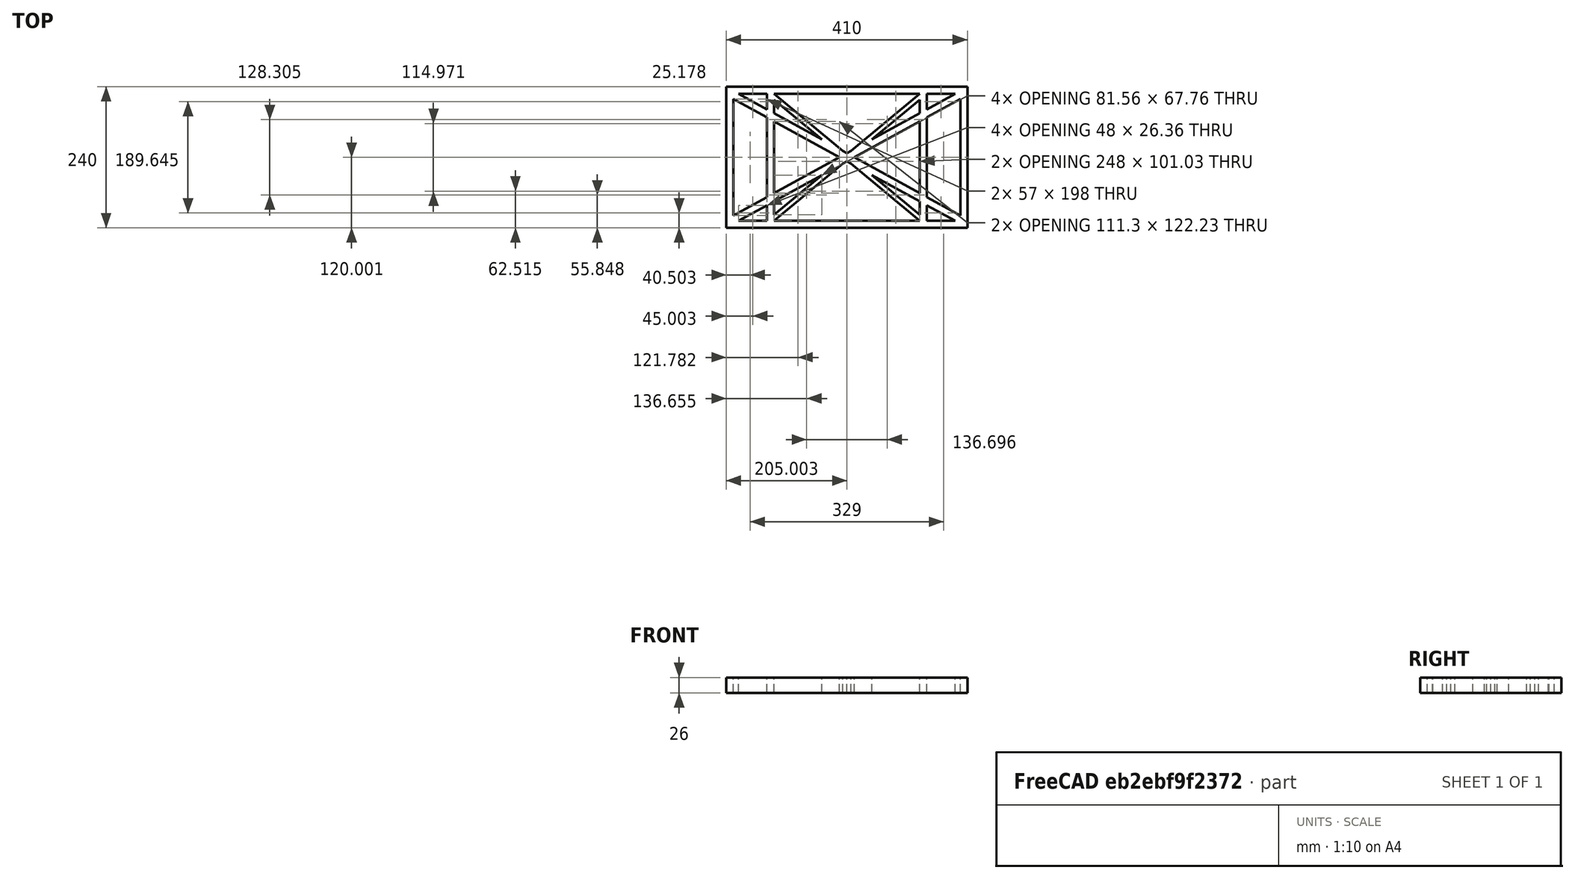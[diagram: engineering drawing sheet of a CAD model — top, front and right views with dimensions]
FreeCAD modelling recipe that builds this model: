
FCSTD DOCUMENT  (FreeCAD 0.19R0.19.2)
Label: laptopStand032
License: All rights reserved
LicenseURL: http://en.wikipedia.org/wiki/All_rights_reserved
objects: Sketcher::SketchObject×3, Part::Extrusion×1
note: 4 computed .brp shape members not serialized (recipe doc carries the construction recipe); baked Part::Feature solids carry a one-line shape summary decoded from their .brp

FEATURE [Sketcher::SketchObject] Sketch
  FullyConstrained = true
  sketch-geometry (52):
    g0: LineSegment StartX=-22.9272 StartY=136.221 StartZ=0 EndX=-22.9272 EndY=-103.779 EndZ=0
    g1: LineSegment StartX=-22.9272 StartY=136.221 StartZ=0 EndX=387.073 EndY=136.221 EndZ=0
    g2: LineSegment StartX=-22.9272 StartY=-103.779 StartZ=0 EndX=387.073 EndY=-103.779 EndZ=0
    g3: LineSegment StartX=387.073 StartY=136.221 StartZ=0 EndX=387.073 EndY=-103.779 EndZ=0
    g4: LineSegment StartX=375.073 StartY=115.221 StartZ=0 EndX=318.073 EndY=83.9235 EndZ=0
    g5: LineSegment StartX=-10.9272 StartY=-82.7794 StartZ=0 EndX=46.0728 EndY=-51.4823 EndZ=0
    g6: LineSegment StartX=-1.92719 StartY=124.221 StartZ=0 EndX=46.0728 EndY=97.8651 EndZ=0
    g7: LineSegment StartX=366.073 StartY=-91.7794 StartZ=0 EndX=318.073 EndY=-65.424 EndZ=0
    g8: LineSegment StartX=-10.9272 StartY=115.221 StartZ=0 EndX=-10.9272 EndY=-82.7794 EndZ=0
    g9: LineSegment StartX=375.073 StartY=-82.7794 StartZ=0 EndX=375.073 EndY=115.221 EndZ=0
    g10: LineSegment StartX=-1.92719 StartY=-91.7794 StartZ=0 EndX=46.0728 EndY=-91.7794 EndZ=0
    g11: LineSegment StartX=318.073 StartY=124.221 StartZ=0 EndX=366.073 EndY=124.221 EndZ=0
    g12: LineSegment StartX=306.073 StartY=-81.8102 StartZ=0 EndX=224.513 EndY=-14.0532 EndZ=0
    g13: LineSegment StartX=58.0728 StartY=114.251 StartZ=0 EndX=139.632 EndY=46.4944 EndZ=0
    g14: LineSegment StartX=306.073 StartY=124.221 StartZ=0 EndX=189.124 EndY=27.0628 EndZ=0
    g15: LineSegment StartX=58.0728 StartY=-91.7794 StartZ=0 EndX=175.022 EndY=5.37834 EndZ=0
    g16: LineSegment StartX=46.0728 StartY=124.221 StartZ=0 EndX=46.0728 EndY=97.8651 EndZ=0
    g17: LineSegment StartX=58.0728 StartY=-81.8102 StartZ=0 EndX=58.0728 EndY=-58.8351 EndZ=0
    g18: LineSegment StartX=318.073 StartY=124.221 StartZ=0 EndX=318.073 EndY=97.8651 EndZ=0
    g19: LineSegment StartX=306.073 StartY=114.251 StartZ=0 EndX=306.073 EndY=91.2763 EndZ=0
    g20: LineSegment StartX=182.073 StartY=23.1914 StartZ=0 EndX=189.124 EndY=27.0628 EndZ=0
    g21: LineSegment StartX=182.073 StartY=9.24976 StartZ=0 EndX=175.022 EndY=5.37834 EndZ=0
    g22: LineSegment StartX=224.513 StartY=46.4944 StartZ=0 EndX=306.073 EndY=114.251 EndZ=0
    g23: LineSegment StartX=175.022 StartY=27.0628 StartZ=0 EndX=58.0728 EndY=124.221 EndZ=0
    g24: LineSegment StartX=169.377 StartY=16.2206 StartZ=0 EndX=58.0728 EndY=77.3346 EndZ=0
    g25: LineSegment StartX=139.632 StartY=-14.0532 StartZ=0 EndX=58.0728 EndY=-81.8102 EndZ=0
    g26: LineSegment StartX=194.768 StartY=16.2206 StartZ=0 EndX=306.073 EndY=-44.8935 EndZ=0
    g27: LineSegment StartX=224.513 StartY=46.4944 StartZ=0 EndX=306.073 EndY=91.2763 EndZ=0
    g28: LineSegment StartX=175.022 StartY=27.0628 StartZ=0 EndX=182.073 EndY=23.1914 EndZ=0
    g29: LineSegment StartX=139.632 StartY=-14.0532 StartZ=0 EndX=58.0728 EndY=-58.8351 EndZ=0
    g30: LineSegment StartX=189.124 StartY=5.37834 StartZ=0 EndX=182.073 EndY=9.24976 EndZ=0
    g31: LineSegment StartX=189.124 StartY=5.37834 StartZ=0 EndX=306.073 EndY=-91.7794 EndZ=0
    g32: LineSegment StartX=306.073 StartY=77.3346 StartZ=0 EndX=306.073 EndY=-44.8935 EndZ=0
    g33: LineSegment StartX=318.073 StartY=83.9235 StartZ=0 EndX=318.073 EndY=-51.4823 EndZ=0
    g34: LineSegment StartX=318.073 StartY=97.8651 StartZ=0 EndX=366.073 EndY=124.221 EndZ=0
    g35: LineSegment StartX=306.073 StartY=77.3346 StartZ=0 EndX=194.768 EndY=16.2206 EndZ=0
    g36: LineSegment StartX=306.073 StartY=-58.8351 StartZ=0 EndX=224.513 EndY=-14.0532 EndZ=0
    g37: LineSegment StartX=306.073 StartY=-58.8351 StartZ=0 EndX=306.073 EndY=-81.8102 EndZ=0
    g38: LineSegment StartX=318.073 StartY=-51.4823 StartZ=0 EndX=375.073 EndY=-82.7794 EndZ=0
    g39: LineSegment StartX=318.073 StartY=-65.424 StartZ=0 EndX=318.073 EndY=-91.7794 EndZ=0
    g40: LineSegment StartX=306.073 StartY=124.221 StartZ=0 EndX=58.0728 EndY=124.221 EndZ=0
    g41: LineSegment StartX=318.073 StartY=-91.7794 StartZ=0 EndX=366.073 EndY=-91.7794 EndZ=0
    g42: LineSegment StartX=58.0728 StartY=-91.7794 StartZ=0 EndX=306.073 EndY=-91.7794 EndZ=0
    g43: LineSegment StartX=58.0728 StartY=-44.8935 StartZ=0 EndX=58.0728 EndY=77.3346 EndZ=0
    g44: LineSegment StartX=46.0728 StartY=-65.424 StartZ=0 EndX=-1.92719 EndY=-91.7794 EndZ=0
    g45: LineSegment StartX=46.0728 StartY=-65.424 StartZ=0 EndX=46.0728 EndY=-91.7794 EndZ=0
    g46: LineSegment StartX=58.0728 StartY=-44.8935 StartZ=0 EndX=169.377 EndY=16.2206 EndZ=0
    g47: LineSegment StartX=58.0728 StartY=91.2763 StartZ=0 EndX=58.0728 EndY=114.251 EndZ=0
    g48: LineSegment StartX=46.0728 StartY=83.9235 StartZ=0 EndX=46.0728 EndY=-51.4823 EndZ=0
    g49: LineSegment StartX=46.0728 StartY=124.221 StartZ=0 EndX=-1.92719 EndY=124.221 EndZ=0
    g50: LineSegment StartX=58.0728 StartY=91.2763 StartZ=0 EndX=139.632 EndY=46.4944 EndZ=0
    g51: LineSegment StartX=46.0728 StartY=83.9235 StartZ=0 EndX=-10.9272 EndY=115.221 EndZ=0
  constraints (102):
    c: Vertical(g0)
    c: Distance(g0) = 240
    c: Horizontal(g1)
    c: Distance(g1) = 410
    c: Coincident(g1,g0)
    c: Coincident(g2,g0)
    c: Horizontal(g2)
    c: Coincident(g3,g1)
    c: Vertical(g3)
    c: Coincident(g2,g3)
    c: Block(g1)
    c: Horizontal(g10)
    c: Horizontal(g11)
    c: PointOnObject(g35,g6)
    c: Coincident(g28,g20)
    c: Coincident(g30,g21)
    c: Tangent(g7,g24)
    c: PointOnObject(g24,g5)
    c: PointOnObject(g26,g4)
    c: Coincident(g20,g14)
    c: Tangent(g20,g27)
    c: Coincident(g50,g13)
    c: Coincident(g28,g23)
    c: Coincident(g22,g27)
    c: Coincident(g21,g15)
    c: Coincident(g29,g25)
    c: Tangent(g21,g29)
    c: Coincident(g36,g12)
    c: Coincident(g31,g30)
    c: Coincident(g22,g19)
    c: Tangent(g19,g32)
    c: Tangent(g18,g33)
    c: Coincident(g27,g19)
    c: Tangent(g27,g34)
    c: Coincident(g4,g33)
    c: Coincident(g35,g32)
    c: Tangent(g4,g35)
    c: Coincident(g37,g12)
    c: Tangent(g7,g36)
    c: Tangent(g32,g37)
    c: Coincident(g26,g32)
    c: Tangent(g26,g38)
    c: Coincident(g33,g38)
    c: Coincident(g39,g7)
    c: Tangent(g33,g39)
    c: Coincident(g25,g17)
    c: Tangent(g17,g43)
    c: Coincident(g29,g17)
    c: Tangent(g29,g44)
    c: Coincident(g45,g44)
    c: Tangent(g16,g45)
    c: Coincident(g5,g48)
    c: Coincident(g46,g43)
    c: Tangent(g5,g46)
    c: Tangent(g43,g47)
    c: Tangent(g16,g48)
    c: Coincident(g13,g47)
    c: PointOnObject(g40,g23)
    c: Tangent(g40,g49)
    c: Coincident(g6,g16)
    c: Coincident(g50,g47)
    c: Tangent(g6,g50)
    c: Coincident(g24,g43)
    c: Coincident(g51,g48)
    c: Tangent(g24,g51)
    c: Block(g23)
    c: Block(g14)
    c: Block(g20)
    c: Block(g40)
    c: Block(g18)
    c: Block(g34)
    c: Block(g4)
    c: Block(g38)
    c: Block(g9)
    c: Block(g36)
    c: Block(g37)
    c: Block(g7)
    c: Block(g39)
    c: Block(g22)
    c: Block(g31)
    c: Block(g42)
    c: Block(g21)
    c: Block(g15)
    c: Block(g29)
    c: Block(g25)
    c: Block(g45)
    c: Block(g44)
    c: Block(g5)
    c: Block(g8)
    c: Block(g51)
    c: Block(g6)
    c: Block(g16)
    c: Block(g13)
    c: Block(g47)
    c: Block(g35)
    c: Block(g32)
    c: Block(g24)
    c: Block(g46)
    c: Block(g49)
    c: Block(g11)
    c: Block(g41)
    c: Block(g10)
FEATURE [Part::Extrusion] Extrude
  Base = -> Sketch
  Dir = (0,0,1)
  DirMode = 2
  FaceMakerClass = Part::FaceMakerBullseye
  LengthFwd = 26
  LengthRev = 0
  Solid = true
  Symmetric = false
FEATURE [Sketcher::SketchObject] Sketch001
  FullyConstrained = true
  MapMode = 4
  Placement = pos=(0,0,0) rot=(0.57735,0.57735,0.57735;2.0944rad)
  Support = -> [Sketch]
  sketch-geometry (36):
    g0: LineSegment StartX=17.2232 StartY=-16.0875 StartZ=0 EndX=117.223 EndY=-16.0875 EndZ=0
    g1: LineSegment StartX=17.2232 StartY=-16.0875 StartZ=0 EndX=17.2232 EndY=-19.0875 EndZ=0
    g2: LineSegment StartX=117.223 StartY=-16.0875 StartZ=0 EndX=117.223 EndY=-19.0875 EndZ=0
    g3: BSplineCurve PolesCount=3 KnotsCount=2 Degree=2 IsPeriodic=0
    g4: LineSegment StartX=17.2232 StartY=-19.0875 StartZ=0 EndX=29.8094 EndY=-19.0875 EndZ=0
    g5: ArcOfCircle CenterX=73.122 CenterY=-32.2909 CenterZ=0 NormalX=0 NormalY=0 NormalZ=1 AngleXU=0 Radius=13 StartAngle=5.92268 EndAngle=9.06428
    g6: LineSegment StartX=85.2864 StartY=-36.8765 StartZ=0 EndX=78.9505 EndY=-53.7246 EndZ=0
    g7: LineSegment StartX=60.9577 StartY=-27.7052 StartZ=0 EndX=54.6191 EndY=-44.5532 EndZ=0
    g8: ArcOfCircle CenterX=66.7816 CenterY=-49.1439 CenterZ=0 NormalX=0 NormalY=0 NormalZ=1 AngleXU=0 Radius=13 StartAngle=2.78068 EndAngle=5.92131
    g9: ArcOfCircle CenterX=55.9263 CenterY=-78.1807 CenterZ=0 NormalX=0 NormalY=0 NormalZ=1 AngleXU=0 Radius=13 StartAngle=5.92268 EndAngle=9.06428
    g10: LineSegment StartX=68.0907 StartY=-82.7664 StartZ=0 EndX=61.7547 EndY=-99.6148 EndZ=0
    g11: ArcOfCircle CenterX=49.5884 CenterY=-95.0342 CenterZ=0 NormalX=0 NormalY=0 NormalZ=1 AngleXU=0 Radius=13 StartAngle=2.78068 EndAngle=5.92131
    g12: LineSegment StartX=43.7619 StartY=-73.595 StartZ=0 EndX=37.426 EndY=-90.4435 EndZ=0
    g13: ArcOfCircle CenterX=38.7206 CenterY=-124.067 CenterZ=0 NormalX=0 NormalY=0 NormalZ=1 AngleXU=0 Radius=13 StartAngle=5.92268 EndAngle=9.06428
    g14: LineSegment StartX=26.5562 StartY=-119.481 StartZ=0 EndX=20.2251 EndY=-136.329 EndZ=0
    g15: ArcOfCircle CenterX=32.3875 CenterY=-140.92 CenterZ=0 NormalX=0 NormalY=0 NormalZ=1 AngleXU=0 Radius=13 StartAngle=2.78068 EndAngle=5.92131
    g16: LineSegment StartX=50.885 StartY=-128.652 StartZ=0 EndX=44.549 EndY=-145.5 EndZ=0
    g17: ArcOfCircle CenterX=21.4715 CenterY=-169.934 CenterZ=0 NormalX=0 NormalY=0 NormalZ=1 AngleXU=0 Radius=13 StartAngle=5.92268 EndAngle=9.06428
    g18: LineSegment StartX=9.3071 StartY=-165.349 StartZ=0 EndX=2.97115 EndY=-182.197 EndZ=0
    g19: ArcOfCircle CenterX=15.1336 CenterY=-186.787 CenterZ=0 NormalX=0 NormalY=0 NormalZ=1 AngleXU=0 Radius=13 StartAngle=2.78068 EndAngle=5.92131
    g20: LineSegment StartX=33.6358 StartY=-174.52 StartZ=0 EndX=27.2999 EndY=-191.368 EndZ=0
    g21: LineSegment StartX=94.6577 StartY=-26.1351 StartZ=0 EndX=25.4551 EndY=-210.153 EndZ=0
    g22-g25: Circle x4 (B-spline internal-alignment scaffolding for g26; pole/knot coordinates omitted)
    g26: BSplineCurve PolesCount=4 KnotsCount=2 Degree=3 IsPeriodic=0
    g27: GeomPoint X=28.8094 Y=-19.0875 Z=0
    g28: GeomPoint X=47.0443 Y=-50.4712 Z=0
    g29: Circle CenterX=53.5586 CenterY=-23.2695 CenterZ=0 NormalX=0 NormalY=0 NormalZ=1 AngleXU=0 Radius=3.24518
    g30: LineSegment StartX=25.4551 StartY=-210.153 StartZ=0 EndX=44.1752 EndY=-217.193 EndZ=0
    g31: LineSegment StartX=44.1752 StartY=-217.193 StartZ=0 EndX=43.1192 EndY=-220.001 EndZ=0
    g32: LineSegment StartX=-195.441 StartY=-127.082 StartZ=0 EndX=-196.497 EndY=-129.89 EndZ=0
    g33: LineSegment StartX=-196.497 StartY=-129.89 StartZ=0 EndX=43.1192 EndY=-220.001 EndZ=0
    g34: LineSegment StartX=-8.24091 StartY=-197.481 StartZ=0 EndX=9.35893 EndY=-150.681 EndZ=0
    g35: LineSegment StartX=9.35893 StartY=-150.681 StartZ=0 EndX=47.0443 EndY=-50.4712 EndZ=0
  constraints (71):
    c: Horizontal(g0)
    c: Distance(g0) = 100
    c: Block(g0)
    c: Coincident(g1,g0)
    c: Vertical(g1)
    c: Distance(g1) = 3
    c: Coincident(g2,g0)
    c: Vertical(g2)
    c: Distance(g2) = 3
    c: Block(g3)
    c: Coincident(g3,g2)
    c: Coincident(g4,g1)
    c: Horizontal(g4)
    c: Block(g5)
    c: Distance(g6) = 18
    c: Coincident(g6,g5)
    c: Coincident(g7,g5)
    c: Block(g8)
    c: Coincident(g8,g7)
    c: Block(g7)
    c: Coincident(g10,g9)
    c: Coincident(g12,g9)
    c: Block(g11)
    c: Coincident(g11,g12)
    c: Block(g12)
    c: Block(g9)
    c: Block(g10)
    c: Coincident(g16,g13)
    c: Coincident(g14,g13)
    c: Block(g15)
    c: Coincident(g15,g14)
    c: Block(g14)
    c: Block(g13)
    c: Coincident(g20,g17)
    c: Coincident(g18,g17)
    c: Block(g19)
    c: Coincident(g19,g18)
    c: Block(g18)
    c: Block(g17)
    c: Distance(g20) = 18
    c: Block(g20)
    c: Block(g16)
    c: Coincident(g21,g3)
    c: Block(g21)
    c: Block(g6)
    c: Weight(g22) = 1
    c: Equal(g22,g23)
    c: Equal(g22,g24)
    c: Equal(g22,g25)
    c: InternalAlignment(g22-g25 -> g26) x4
    c: InternalAlignment(g27,g26)
    c: InternalAlignment(g28,g26)
    c: PointOnObject(g4,g22)
    c: Block(g26)
    c: Block(g29)
    c: Distance(g30) = 20
    c: Perpendicular(g21,g30)
    c: Coincident(g30,g21)
    c: Distance(g31) = 3
    c: Perpendicular(g30,g31)
    c: Distance(g32) = 3
    c: Coincident(g33,g32)
    c: Coincident(g33,g31)
    c: Distance(g34) = 50
    c: Parallel(g21,g34)
    c: Block(g33)
    c: Block(g32)
    c: Coincident(g35,g34)
    c: Coincident(g35,g26)
    c: Block(g35)
    c: Block(g31)
FEATURE [Sketcher::SketchObject] Sketch002
  FullyConstrained = true
  Placement = pos=(0,0,0) rot=(-1,0,0;4.71239rad)
